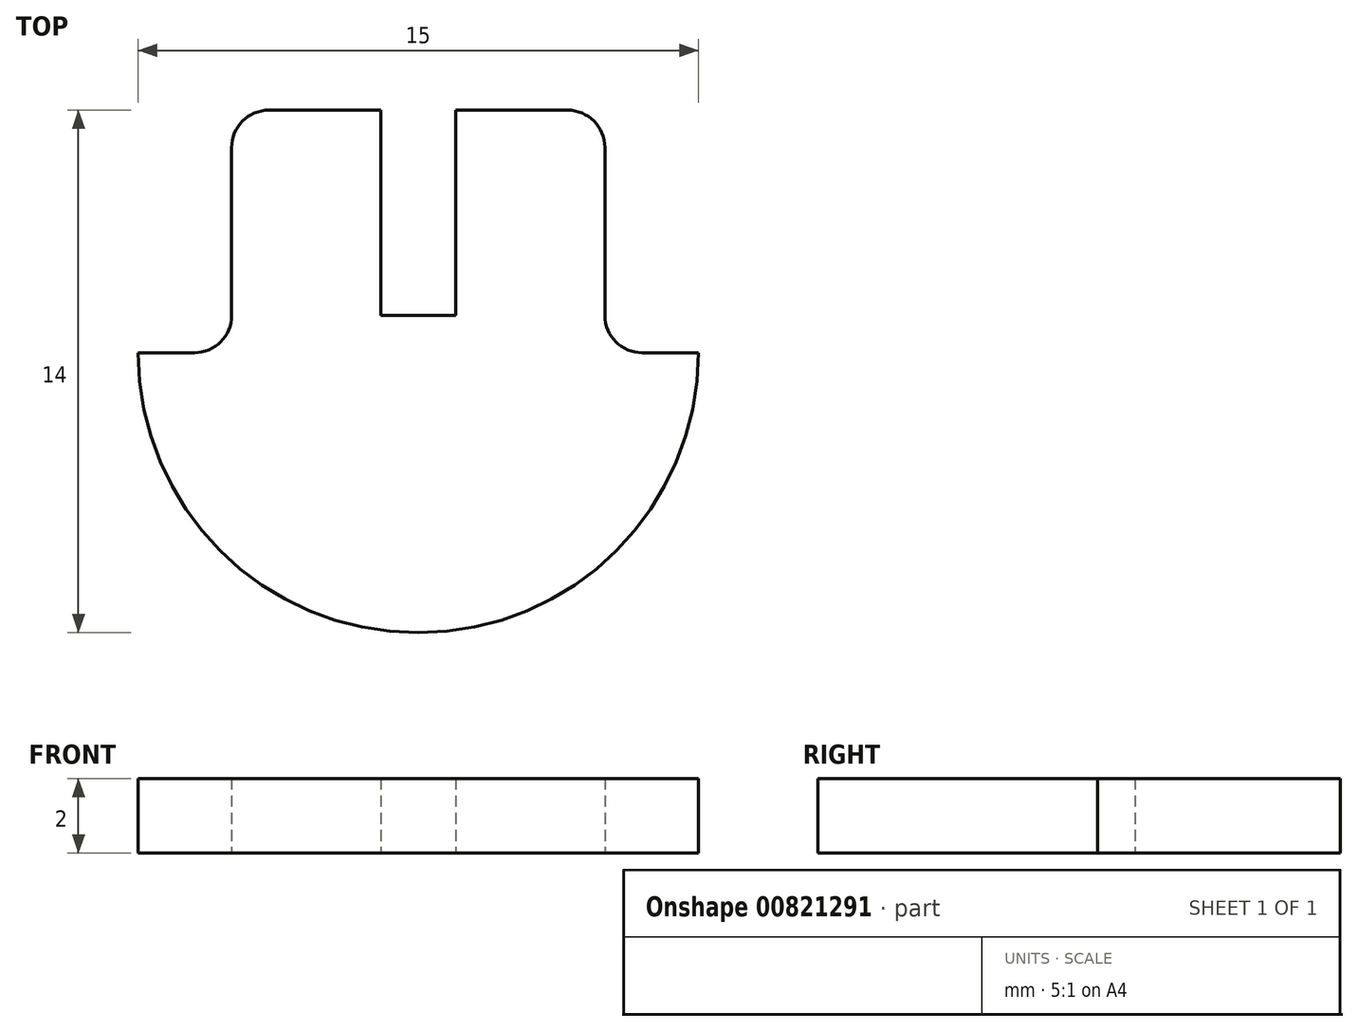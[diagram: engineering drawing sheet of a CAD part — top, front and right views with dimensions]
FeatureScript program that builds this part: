
annotation { "Feature Type Name" : "Feature", "Feature Type Description" : "" }
export const myFeature = defineFeature(function(context is Context, id is Id, definition is map)
    precondition{}
    {
        {
            var Q0;
            Q0=qCreatedBy(makeId("Top.planeOp"),FACE);
            var sketch = newSketch(context, id + "F0", { "sketchPlane" : qUnion([Q0])});
            skArc(sketch, "E0", {"start": v(-7.5, 0) * mm, "mid": v(0, -7.5) * mm, "end": v(7.5, 0) * mm});
            skLineSegment(sketch, "E1", {"start": v(-7.5, 0) * mm, "end": v(-6, 0) * mm});
            skLineSegment(sketch, "E2", {"start": v(7.5, 0) * mm, "end": v(6, 0) * mm});
            skLineSegment(sketch, "E3", {"start": v(-4, 6.5) * mm, "end": v(-1, 6.5) * mm});
            skLineSegment(sketch, "E4", {"start": v(-5, 5.5) * mm, "end": v(-5, 1) * mm});
            skLineSegment(sketch, "E5", {"start": v(5, 5.5) * mm, "end": v(5, 1) * mm});
            skLineSegment(sketch, "E6", {"start": v(-1, 6.5) * mm, "end": v(-1, 1) * mm});
            skLineSegment(sketch, "E7", {"start": v(1, 6.5) * mm, "end": v(1, 1) * mm});
            skLineSegment(sketch, "E8.trimOffspring", {"start": v(-6, 0) * mm, "end": v(-7.5, 0) * mm});
            skLineSegment(sketch, "E9.trimOffspring", {"start": v(1, 6.5) * mm, "end": v(4, 6.5) * mm});
            skPoint(sketch, "E10.visualSharp", {"position": v(-5, 6.5) * mm});
            skArc(sketch, "E10.filletArc", {"start": v(-4, 6.5) * mm, "mid": v(-4.7, 6.2) * mm, "end": v(-5, 5.5) * mm});
            skPoint(sketch, "E11.visualSharp", {"position": v(5, 6.5) * mm});
            skArc(sketch, "E11.filletArc", {"start": v(5, 5.5) * mm, "mid": v(4.7, 6.2) * mm, "end": v(4, 6.5) * mm});
            skArc(sketch, "E12.filletArc", {"start": v(-6, 0) * mm, "mid": v(-5.3, 0.3) * mm, "end": v(-5, 1) * mm});
            skArc(sketch, "E13.filletArc", {"start": v(5, 1) * mm, "mid": v(5.3, 0.3) * mm, "end": v(6, 0) * mm});
            skLineSegment(sketch, "E14.trimOffspring", {"start": v(6, 0) * mm, "end": v(7.5, 0) * mm});
            skLineSegment(sketch, "E15", {"start": v(-1, 1) * mm, "end": v(1, 1) * mm});
            skSolve(sketch);
        }
        {
            var Q0;
            Q0 = qSketchRegion(id + "F0", true);
            extrude(context, id + "F1", {"entities" : qUnion([Q0]), "depth" : 2 * mm, "offsetDistance" : 25 * mm});
        }
    });
